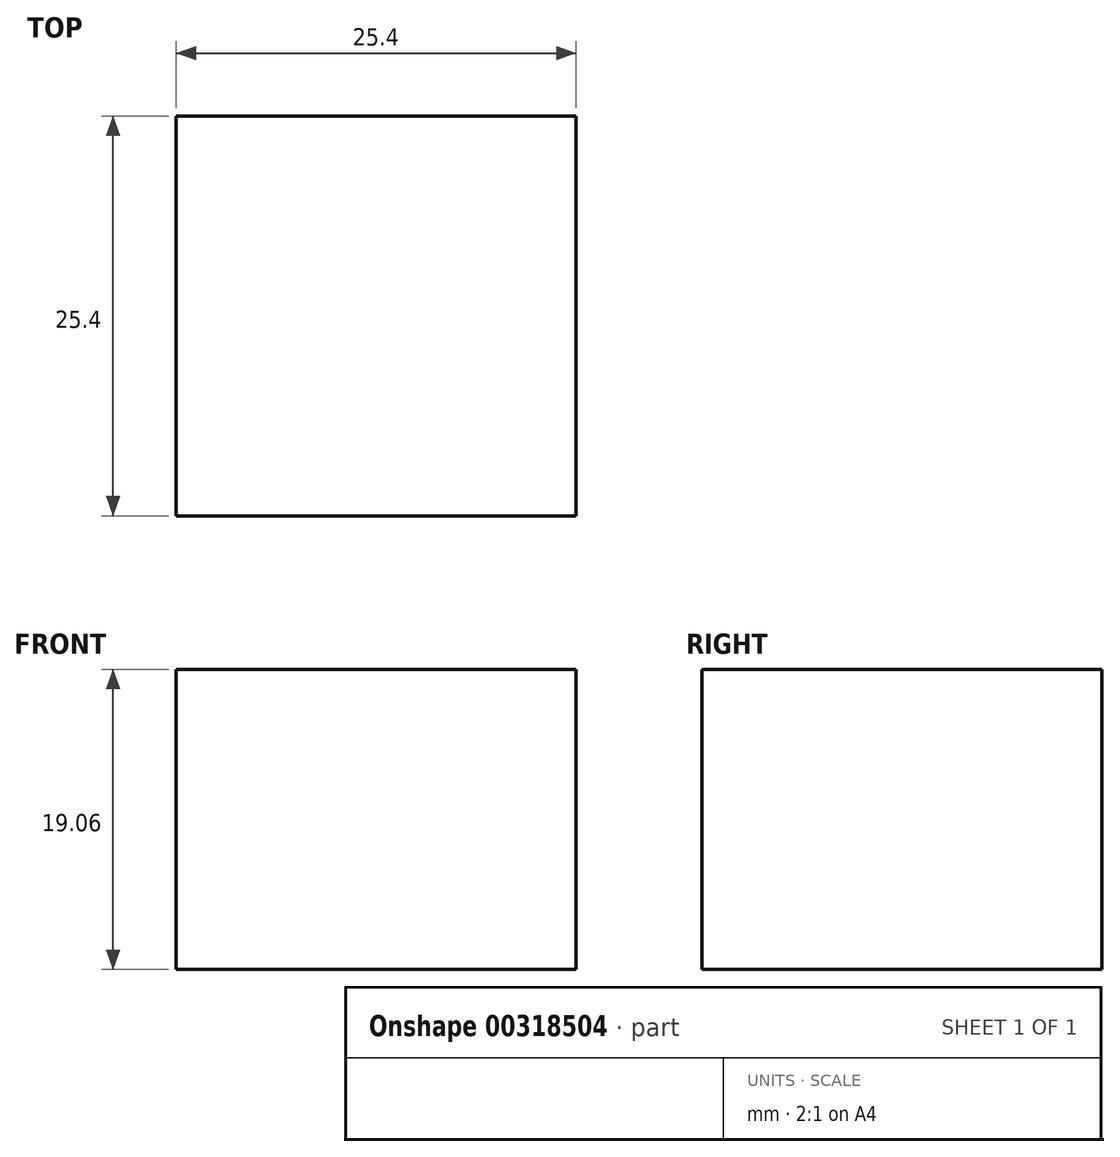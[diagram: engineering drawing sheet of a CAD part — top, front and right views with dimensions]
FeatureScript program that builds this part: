
annotation { "Feature Type Name" : "Feature", "Feature Type Description" : "" }
export const myFeature = defineFeature(function(context is Context, id is Id, definition is map)
    precondition{}
    {
        {
            var Q0;
            Q0=qCreatedBy(makeId("Front.planeOp"),FACE);
            var sketch = newSketch(context, id + "F0", { "sketchPlane" : qUnion([Q0])});
            skLineSegment(sketch, "E0.bottom", {"start": v(12.7, -9.53) * mm, "end": v(-12.7, -9.53) * mm});
            skLineSegment(sketch, "E0.top", {"start": v(12.7, 9.53) * mm, "end": v(-12.7, 9.53) * mm});
            skLineSegment(sketch, "E0.left", {"start": v(12.7, -9.53) * mm, "end": v(12.7, 9.52) * mm});
            skLineSegment(sketch, "E0.right", {"start": v(-12.7, -9.53) * mm, "end": v(-12.7, 9.52) * mm});
            skPoint(sketch, "E0.middle", {"position": v(0, 0) * mm});
            skSolve(sketch);
        }
        {
            var Q0;
            Q0 = qSketchRegion(id + "F0", true);
            extrude(context, id + "F1", {"entities" : qUnion([Q0]), "depth" : 25.4 * mm});
        }
    });
